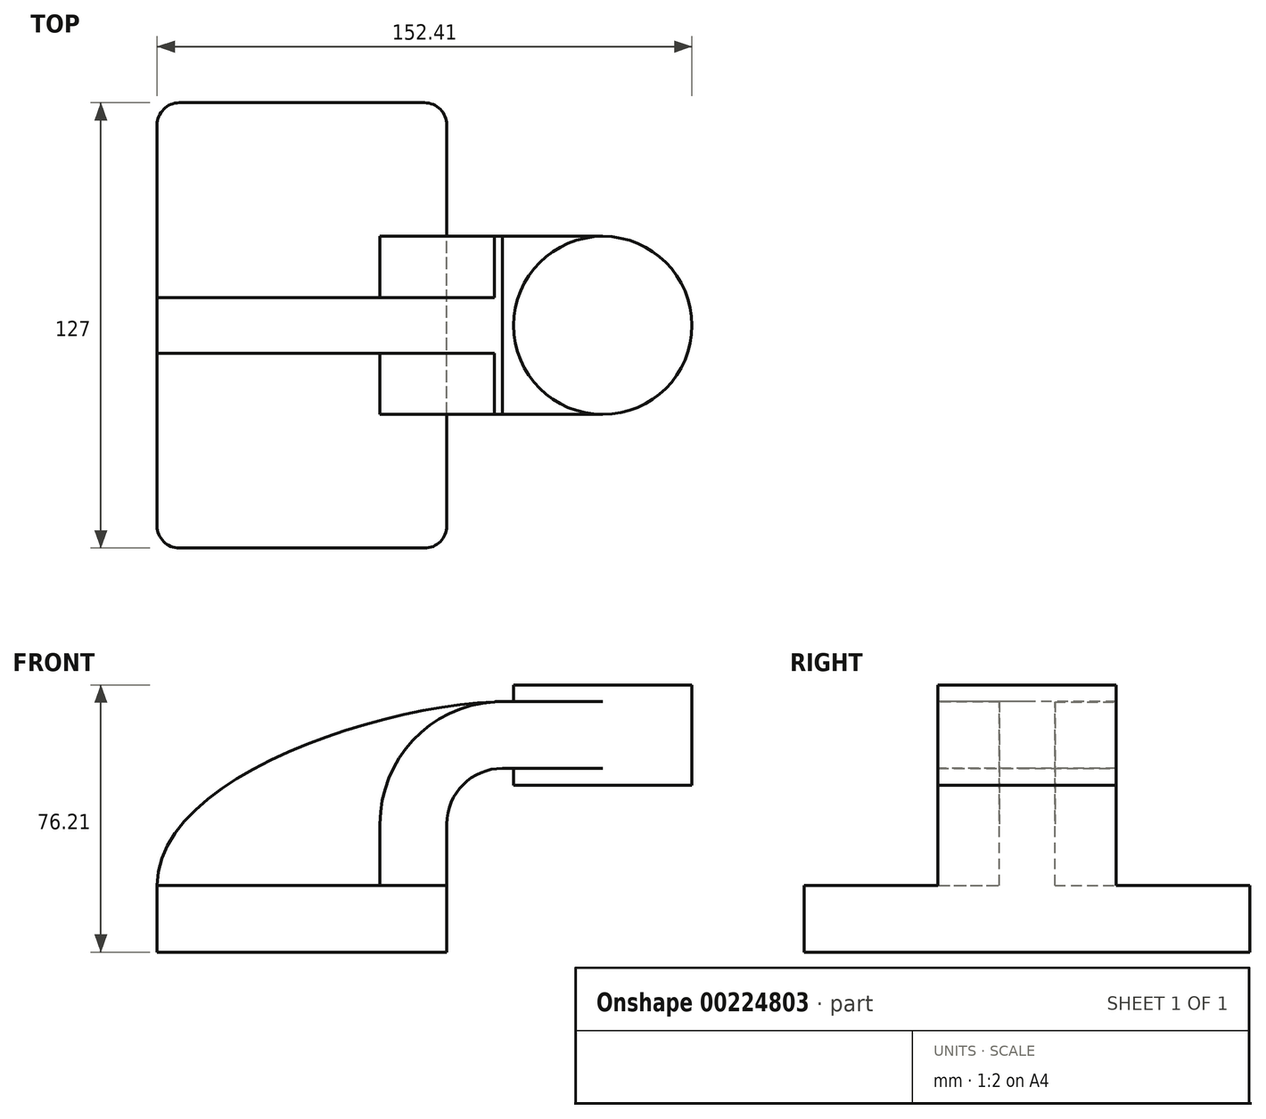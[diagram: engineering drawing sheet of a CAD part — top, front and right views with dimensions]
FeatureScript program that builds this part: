
annotation { "Feature Type Name" : "Feature", "Feature Type Description" : "" }
export const myFeature = defineFeature(function(context is Context, id is Id, definition is map)
    precondition{}
    {
        {
            var Q0;
            Q0=qCreatedBy(makeId("Front.planeOp"),FACE);
            var sketch = newSketch(context, id + "F0", { "sketchPlane" : qUnion([Q0])});
            skLineSegment(sketch, "E0.bottom", {"start": v(41.28, -9.52) * mm, "end": v(-41.28, -9.53) * mm});
            skLineSegment(sketch, "E0.top", {"start": v(41.28, 9.53) * mm, "end": v(-41.28, 9.53) * mm});
            skLineSegment(sketch, "E0.left", {"start": v(41.28, -9.52) * mm, "end": v(41.28, 9.53) * mm});
            skLineSegment(sketch, "E0.right", {"start": v(-41.28, -9.52) * mm, "end": v(-41.28, 9.53) * mm});
            skPoint(sketch, "E0.middle", {"position": v(0, 0) * mm});
            skLineSegment(sketch, "E1.bottom", {"start": v(111.12, 38.1) * mm, "end": v(60.33, 38.1) * mm});
            skLineSegment(sketch, "E1.top", {"start": v(111.12, 66.68) * mm, "end": v(60.33, 66.68) * mm});
            skLineSegment(sketch, "E1.left", {"start": v(111.12, 38.1) * mm, "end": v(111.12, 66.68) * mm});
            skLineSegment(sketch, "E1.right", {"start": v(60.33, 38.1) * mm, "end": v(60.33, 66.68) * mm});
            skPoint(sketch, "E1.middle", {"position": v(85.72, 52.39) * mm});
            skLineSegment(sketch, "E2", {"start": v(41.28, 9.53) * mm, "end": v(41.28, 27) * mm});
            skArc(sketch, "E3", {"start": v(41.27, 27) * mm, "mid": v(45.92, 38.23) * mm, "end": v(57.15, 42.88) * mm});
            skLineSegment(sketch, "E4", {"start": v(57.15, 42.88) * mm, "end": v(85.72, 42.88) * mm});
            skLineSegment(sketch, "E5.0", {"start": v(57.15, 61.93) * mm, "end": v(85.72, 61.93) * mm});
            skArc(sketch, "E5.1", {"start": v(22.23, 27) * mm, "mid": v(32.45, 51.7) * mm, "end": v(57.15, 61.93) * mm});
            skLineSegment(sketch, "E5.2", {"start": v(22.22, 9.53) * mm, "end": v(22.22, 27) * mm});
            skLineSegment(sketch, "E6", {"start": v(85.72, 38.1) * mm, "end": v(85.72, 66.68) * mm});
            skFitSpline(sketch, "E7", {"points": [v(-41.28, 9.52) * mm, v(57.15, 61.93) * mm], "startDerivative": vector(0.3, 92.36) * mm, "endDerivative": vector(105.08, 2.26) * mm});
            skSolve(sketch);
        }
        {
            var Q0;
            Q0=makeQuery(id+"F0.imprint","IMPRINT",FACE,{"disambiguationData":[TD([[makeQuery(id+"F0.imprint","IMPRINT",EDGE,{"derivedFrom":sQuery(id+"F0.wireOp",EDGE,"E0.bottom")}),-1.0]])]});
            extrude(context, id + "F1", {"entities" : qUnion([Q0]), "depth" : 127 * mm, "symmetric" : true});
        }
        {
            var Q0;
            {var subQ1=sQuery(id+"F0.wireOp",EDGE,"E2");Q0=makeQuery(id+"F0.imprint","IMPRINT",FACE,{"disambiguationData":[TD([[makeQuery(id+"F0.imprint","IMPRINT",EDGE,{"derivedFrom":subQ1}),1.0]])]});}
            var Q1;
            {var subQ0=sQuery(id+"F0.wireOp",EDGE,"E4");var subQ1=sQuery(id+"F0.wireOp",EDGE,"E1.right");var subQ2=makeQuery(id+"F0.imprint","INTERSECT",VERTEX,{"derivedFrom":[subQ1,subQ0]});Q1=makeQuery(id+"F0.imprint","IMPRINT",FACE,{"disambiguationData":[TD([[makeQuery(id+"F0.imprint","IMPRINT",EDGE,{"disambiguationData":[TD([[subQ2,-1.0]])],"derivedFrom":subQ1}),-1.0]])]});}
            extrude(context, id + "F2", {"entities" : qUnion([Q0, Q1]), "operationType" : NewBodyOperationType.ADD, "depth" : 50.8 * mm, "symmetric" : true});
        }
        {
            var Q0;
            {var subQ3=sQuery(id+"F0.wireOp",EDGE,"E5.2");Q0=makeQuery(id+"F0.imprint","IMPRINT",FACE,{"disambiguationData":[TD([[makeQuery(id+"F0.imprint","IMPRINT",EDGE,{"derivedFrom":subQ3}),1.0]])]});}
            extrude(context, id + "F3", {"entities" : qUnion([Q0]), "operationType" : NewBodyOperationType.ADD, "depth" : 15.88 * mm, "symmetric" : true});
        }
        {
            var Q0;
            {var subQ0=sQuery(id+"F0.wireOp",EDGE,"E1.left");Q0=makeQuery(id+"F0.imprint","IMPRINT",FACE,{"disambiguationData":[TD([[makeQuery(id+"F0.imprint","IMPRINT",EDGE,{"derivedFrom":subQ0}),1.0]])]});}
            var Q1;
            Q1=sQuery(id+"F0.wireOp",EDGE,"E6");
            revolve(context, id + "F4", {"operationType" : NewBodyOperationType.ADD, "entities" : qUnion([Q0]), "axis" : qUnion([Q1]), "revolveType" : RevolveType.FULL});
        }
        {
            var Q0;
            Q0=makeQuery(id+"F1.opExtrude","CAP_EDGE",EDGE,{"disambiguationData":[OSD([sQuery(id+"F0.wireOp",EDGE,"E0.right")])],"isStart":false});
            var Q1;
            Q1=makeQuery(id+"F1.opExtrude","CAP_EDGE",EDGE,{"disambiguationData":[OSD([sQuery(id+"F0.wireOp",EDGE,"E0.right")])],"isStart":true});
            var Q2;
            Q2=makeQuery(id+"F1.opExtrude","CAP_EDGE",EDGE,{"disambiguationData":[OSD([sQuery(id+"F0.wireOp",EDGE,"E0.left")])],"isStart":true});
            var Q3;
            Q3=makeQuery(id+"F1.opExtrude","CAP_EDGE",EDGE,{"disambiguationData":[OSD([sQuery(id+"F0.wireOp",EDGE,"E0.left")])],"isStart":false});
            fillet(context, id + "F5", {"entities" : qUnion([Q0, Q1, Q2, Q3]), "radius" : 6.35 * mm, "tangentPropagation" : true, "allowEdgeOverflow" : false});
        }
    });
